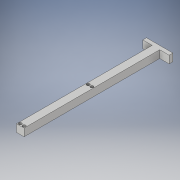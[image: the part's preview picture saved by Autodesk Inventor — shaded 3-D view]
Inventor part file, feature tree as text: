
AUTODESK INVENTOR PART (.ipt)
format: ipt  version: 2017.3 (Build 213256000, 256)  size: 112,640 bytes
history: native  units: in
note: dims shown in document units (in); Inventor stores cm internally (conversion verified against a paired STEP export)
features: sketch x3, extrude x2, hole x1
ambient origin geometry x8: Origin, YZ Plane, XZ Plane, XY Plane, X Axis, Y Axis, Z Axis, Center Point
bodies: Solid1 (feature_tree)
feature tree (6):
  extrude  "Extrusion1"  Depth=0.25in
  extrude  "Extrusion2"  Depth=0.25in
  hole  "Hole1"  [1 undecoded]
  sketch  "Sketch1"  dims[d0=0.875in d1=0.25in]
  sketch  "Sketch2"  dims[d2=0.125in d3=0.0in d4=0.25in]
  sketch  "Sketch3"  dims[d5=4.5in d6=0.0in d7=0.098in d8=0.25in d9=0.375in d10=0.25in d11=0.5635in d12=0.375in d13=0.8108in]
note: 1 required parameter value undecoded (feature->parameter linkage not recoverable at this tier; creation-order binding heuristic only, values carry confidence <= 0.55)
